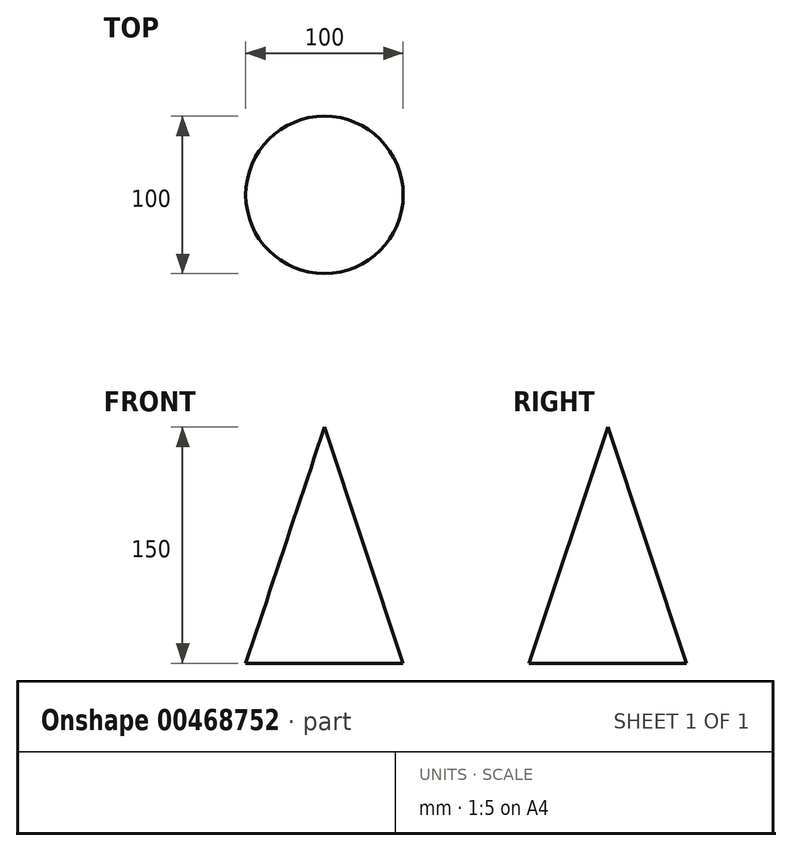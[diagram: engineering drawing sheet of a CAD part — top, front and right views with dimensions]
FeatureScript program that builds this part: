
annotation { "Feature Type Name" : "Feature", "Feature Type Description" : "" }
export const myFeature = defineFeature(function(context is Context, id is Id, definition is map)
    precondition{}
    {
        {
            var Q0;
            Q0=qCreatedBy(makeId("Front.planeOp"),FACE);
            var sketch = newSketch(context, id + "F0", { "sketchPlane" : qUnion([Q0])});
            skLineSegment(sketch, "E0.bottom", {"start": v(0, 0) * mm, "end": v(-50, 0) * mm});
            skLineSegment(sketch, "E0.left", {"start": v(0, 0) * mm, "end": v(0, 150) * mm});
            skLineSegment(sketch, "E1", {"start": v(-50, 0) * mm, "end": v(0, 150) * mm});
            skSolve(sketch);
        }
        {
            var Q0;
            Q0=qSketchRegion(id+"F0",true);
            var Q1;
            Q1=sQuery(id+"F0.wireOp",EDGE,"E0.left");
            revolve(context, id + "F1", {"entities" : qUnion([Q0]), "axis" : qUnion([Q1]), "revolveType" : RevolveType.FULL});
        }
    });
